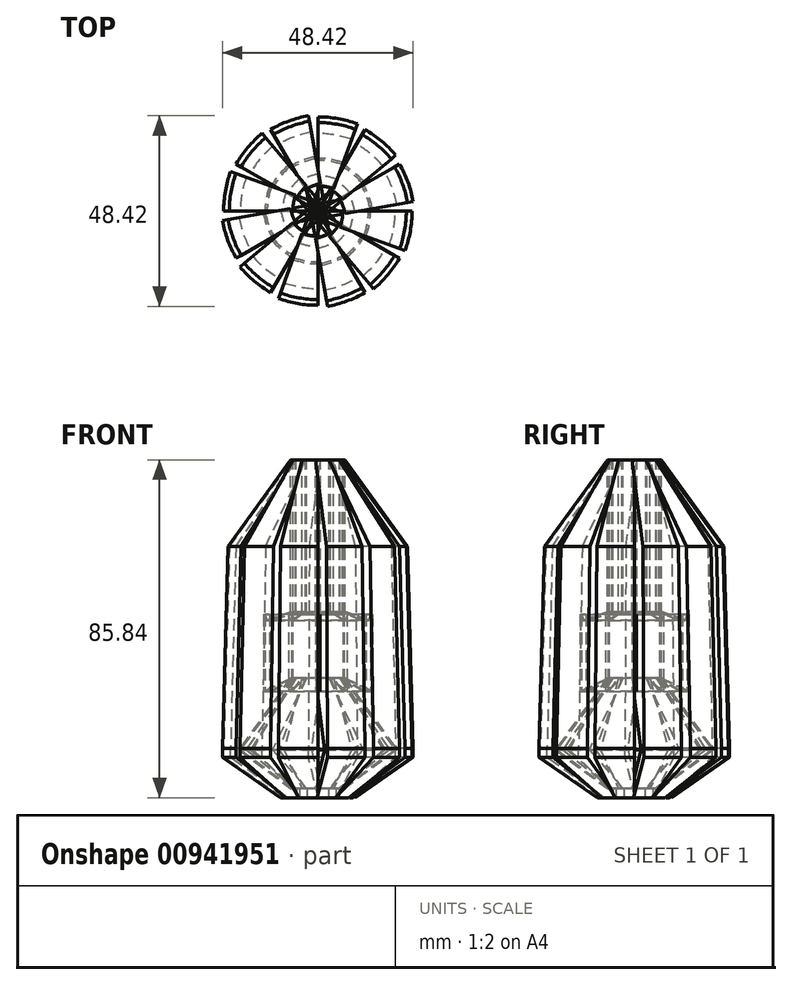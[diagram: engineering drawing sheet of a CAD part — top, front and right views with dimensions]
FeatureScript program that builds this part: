
annotation { "Feature Type Name" : "Feature", "Feature Type Description" : "" }
export const myFeature = defineFeature(function(context is Context, id is Id, definition is map)
    precondition{}
    {
        {
            var Q0;
            Q0=qCreatedBy(makeId("Front.planeOp"),FACE);
            var sketch = newSketch(context, id + "F0", { "sketchPlane" : qUnion([Q0])});
            skLineSegment(sketch, "E0", {"start": v(0, -22.94) * mm, "end": v(14.3, -22.94) * mm});
            skLineSegment(sketch, "E1", {"start": v(14.3, -22.94) * mm, "end": v(29.32, -12.66) * mm});
            skLineSegment(sketch, "E2", {"start": v(29.32, -12.66) * mm, "end": v(29.32, -10.4) * mm});
            skLineSegment(sketch, "E3", {"start": v(27.86, 40.93) * mm, "end": v(29.32, -10.4) * mm});
            skLineSegment(sketch, "E4", {"start": v(27.86, 40.93) * mm, "end": v(11.74, 62.9) * mm});
            skLineSegment(sketch, "E5", {"start": v(11.74, 23.63) * mm, "end": v(11.74, 62.9) * mm});
            skLineSegment(sketch, "E6", {"start": v(11.74, 23.63) * mm, "end": v(11.95, 24.24) * mm});
            skLineSegment(sketch, "E7", {"start": v(18.24, 22.08) * mm, "end": v(11.95, 24.24) * mm});
            skLineSegment(sketch, "E8", {"start": v(18.77, 23.63) * mm, "end": v(18.24, 22.08) * mm});
            skLineSegment(sketch, "E9", {"start": v(18.77, 23.63) * mm, "end": v(18.77, 4.11) * mm});
            skLineSegment(sketch, "E10", {"start": v(18.77, 4.11) * mm, "end": v(11.74, 7.47) * mm});
            skLineSegment(sketch, "E11", {"start": v(11.74, 7.47) * mm, "end": v(25.07, -10.69) * mm});
            skLineSegment(sketch, "E12", {"start": v(25.07, -10.69) * mm, "end": v(25.07, -10.8) * mm});
            skLineSegment(sketch, "E13", {"start": v(25.07, -10.8) * mm, "end": v(11.74, -20.57) * mm});
            skLineSegment(sketch, "E14", {"start": v(11.74, -20.57) * mm, "end": v(0, -20.57) * mm});
            skLineSegment(sketch, "E15", {"start": v(0, -20.57) * mm, "end": v(0, -22.94) * mm});
            skSolve(sketch);
        }
        {
            var Q0;
            Q0=qCreatedBy(makeId("Front.planeOp"),FACE);
            var sketch = newSketch(context, id + "F1", { "sketchPlane" : qUnion([Q0])});
            skLineSegment(sketch, "E16", {"start": v(5.38, -11.9) * mm, "end": v(5.38, -20.1) * mm});
            skSolve(sketch);
        }
        {
            var Q0;
            Q0 = qSketchRegion(id + "F0", true);
            var Q1;
            Q1=sQuery(id+"F0.wireOp",EDGE,"E15");
            revolve(context, id + "F2", {"surfaceOperationType" : NewSurfaceOperationType.NEW, "entities" : qUnion([Q0]), "axis" : qUnion([Q1]), "revolveType" : RevolveType.ONE_DIRECTION, "angle" : 20 * degree});
        }
        {
            var Q0;
            Q0=makeQuery(id+"F2.opRevolve","SWEPT_BODY",BODY,{"disambiguationData":[OSD([sQuery(id+"F0.wireOp",EDGE,"E0"),sQuery(id+"F0.wireOp",EDGE,"E1"),sQuery(id+"F0.wireOp",EDGE,"E2"),sQuery(id+"F0.wireOp",EDGE,"E3"),sQuery(id+"F0.wireOp",EDGE,"E4"),sQuery(id+"F0.wireOp",EDGE,"E5"),sQuery(id+"F0.wireOp",EDGE,"E6"),sQuery(id+"F0.wireOp",EDGE,"E7"),sQuery(id+"F0.wireOp",EDGE,"E8"),sQuery(id+"F0.wireOp",EDGE,"E9"),sQuery(id+"F0.wireOp",EDGE,"E10"),sQuery(id+"F0.wireOp",EDGE,"E11"),sQuery(id+"F0.wireOp",EDGE,"E12"),sQuery(id+"F0.wireOp",EDGE,"E13"),sQuery(id+"F0.wireOp",EDGE,"E14"),sQuery(id+"F0.wireOp",EDGE,"E15")])]});
            var Q1;
            Q1=sQuery(id+"F1.wireOp",EDGE,"E16");
            circularPattern(context, id + "F3", {"entities" : qUnion([Q0]), "axis" : qUnion([Q1]), "angle" : 360 * degree, "instanceCount" : 12, "equalSpace" : true});
        }
    });
